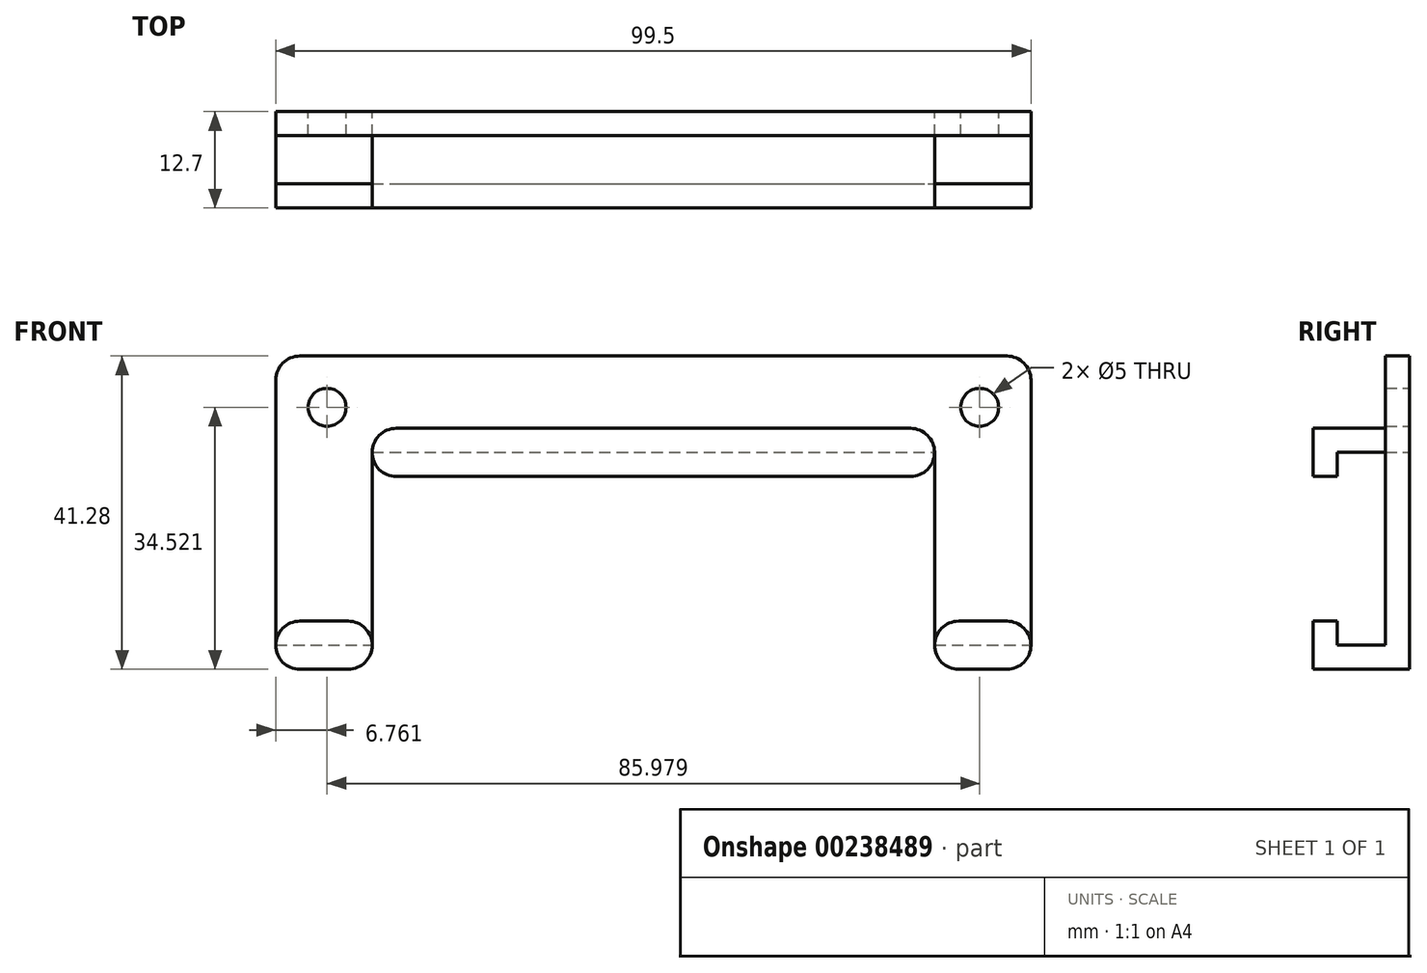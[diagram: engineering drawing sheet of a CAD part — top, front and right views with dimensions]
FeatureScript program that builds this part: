
annotation { "Feature Type Name" : "Feature", "Feature Type Description" : "" }
export const myFeature = defineFeature(function(context is Context, id is Id, definition is map)
    precondition{}
    {
        {
            var Q0;
            Q0=qCreatedBy(makeId("Front.planeOp"),FACE);
            var sketch = newSketch(context, id + "F0", { "sketchPlane" : qUnion([Q0])});
            skLineSegment(sketch, "E0.bottom", {"start": v(-49.75, 20.64) * mm, "end": v(49.75, 20.64) * mm});
            skLineSegment(sketch, "E0.left", {"start": v(-49.75, 20.64) * mm, "end": v(-49.75, -20.64) * mm});
            skLineSegment(sketch, "E0.right", {"start": v(49.75, 20.64) * mm, "end": v(49.75, -20.64) * mm});
            skPoint(sketch, "E0.middle", {"position": v(0, 0) * mm});
            skLineSegment(sketch, "E1", {"start": v(-49.75, -20.64) * mm, "end": v(-37.05, -20.64) * mm});
            skLineSegment(sketch, "E2", {"start": v(49.75, -20.64) * mm, "end": v(37.05, -20.64) * mm});
            skLineSegment(sketch, "E3", {"start": v(-37.05, -20.64) * mm, "end": v(-37.05, 7.94) * mm});
            skLineSegment(sketch, "E4", {"start": v(37.05, -20.64) * mm, "end": v(37.05, 7.94) * mm});
            skLineSegment(sketch, "E5", {"start": v(-37.05, 7.94) * mm, "end": v(37.05, 7.94) * mm});
            skLineSegment(sketch, "E6.bottom", {"start": v(-49.75, 20.64) * mm, "end": v(-42.99, 20.64) * mm, "construction": true});
            skLineSegment(sketch, "E6.top", {"start": v(-49.75, 13.88) * mm, "end": v(-42.99, 13.88) * mm, "construction": true});
            skLineSegment(sketch, "E6.left", {"start": v(-49.75, 20.64) * mm, "end": v(-49.75, 13.88) * mm, "construction": true});
            skLineSegment(sketch, "E6.right", {"start": v(-42.99, 20.64) * mm, "end": v(-42.99, 13.88) * mm, "construction": true});
            skLineSegment(sketch, "E7.bottom", {"start": v(49.75, 20.64) * mm, "end": v(42.99, 20.64) * mm, "construction": true});
            skLineSegment(sketch, "E7.top", {"start": v(49.75, 13.88) * mm, "end": v(42.99, 13.88) * mm, "construction": true});
            skLineSegment(sketch, "E7.left", {"start": v(49.75, 20.64) * mm, "end": v(49.75, 13.88) * mm, "construction": true});
            skLineSegment(sketch, "E7.right", {"start": v(42.99, 20.64) * mm, "end": v(42.99, 13.88) * mm, "construction": true});
            skCircle(sketch, "E8", {"center": v(-42.99, 13.88) * mm, "radius": 2.5 * mm});
            skCircle(sketch, "E9", {"center": v(42.99, 13.88) * mm, "radius": 2.5 * mm});
            skSolve(sketch);
        }
        {
            var Q0;
            Q0=makeQuery(id+"F0.imprint","IMPRINT",FACE,{"disambiguationData":[TD([[makeQuery(id+"F0.imprint","IMPRINT",EDGE,{"derivedFrom":sQuery(id+"F0.wireOp",EDGE,"BnNzGfss-3wFV-08qL-6QTv-cbIZqPfvRORX.bottom")}),1.0]])]});
            var Q1;
            Q1=makeQuery(id+"F0.imprint","IMPRINT",FACE,{"disambiguationData":[TD([[makeQuery(id+"F0.imprint","IMPRINT",EDGE,{"derivedFrom":sQuery(id+"F0.wireOp",EDGE,"E0.bottom")}),-1.0]])]});
            extrude(context, id + "F1", {"entities" : qUnion([Q0, Q1]), "depth" : 3.17 * mm});
        }
        {
            var Q0;
            Q0=makeQuery(id+"F1.opExtrude","CAP_FACE",FACE,{"disambiguationData":[OSD([sQuery(id+"F0.wireOp",EDGE,"E0.bottom"),sQuery(id+"F0.wireOp",EDGE,"E0.left"),sQuery(id+"F0.wireOp",EDGE,"E0.right"),sQuery(id+"F0.wireOp",EDGE,"E1"),sQuery(id+"F0.wireOp",EDGE,"E2"),sQuery(id+"F0.wireOp",EDGE,"E3"),sQuery(id+"F0.wireOp",EDGE,"E4"),sQuery(id+"F0.wireOp",EDGE,"E5"),sQuery(id+"F0.wireOp",EDGE,"E8"),sQuery(id+"F0.wireOp",EDGE,"E9")])],"isStart":false});
            var sketch = newSketch(context, id + "F2", { "sketchPlane" : qUnion([Q0])});
            skLineSegment(sketch, "E10.bottom", {"start": v(-49.75, -20.64) * mm, "end": v(-37.05, -20.64) * mm});
            skLineSegment(sketch, "E10.top", {"start": v(-49.75, -17.46) * mm, "end": v(-37.05, -17.46) * mm});
            skLineSegment(sketch, "E10.left", {"start": v(-49.75, -20.64) * mm, "end": v(-49.75, -17.46) * mm});
            skLineSegment(sketch, "E10.right", {"start": v(-37.05, -20.64) * mm, "end": v(-37.05, -17.46) * mm});
            skLineSegment(sketch, "E11.bottom", {"start": v(37.05, -20.64) * mm, "end": v(49.75, -20.64) * mm});
            skLineSegment(sketch, "E11.top", {"start": v(37.05, -17.46) * mm, "end": v(49.75, -17.46) * mm});
            skLineSegment(sketch, "E11.left", {"start": v(37.05, -20.64) * mm, "end": v(37.05, -17.46) * mm});
            skLineSegment(sketch, "E11.right", {"start": v(49.75, -20.64) * mm, "end": v(49.75, -17.46) * mm});
            skLineSegment(sketch, "E12.bottom", {"start": v(37.05, 7.94) * mm, "end": v(-37.05, 7.94) * mm});
            skLineSegment(sketch, "E12.top", {"start": v(37.05, 11.11) * mm, "end": v(-37.05, 11.11) * mm});
            skLineSegment(sketch, "E12.left", {"start": v(37.05, 7.94) * mm, "end": v(37.05, 11.11) * mm});
            skLineSegment(sketch, "E12.right", {"start": v(-37.05, 7.94) * mm, "end": v(-37.05, 11.11) * mm});
            skSolve(sketch);
        }
        {
            var Q0;
            Q0=makeQuery(id+"F2.imprint","IMPRINT",FACE,{"disambiguationData":[TD([[makeQuery(id+"F2.imprint","IMPRINT",EDGE,{"derivedFrom":sQuery(id+"F2.wireOp",EDGE,"E10.bottom")}),1.0]])]});
            var Q1;
            Q1=makeQuery(id+"F2.imprint","IMPRINT",FACE,{"disambiguationData":[TD([[makeQuery(id+"F2.imprint","IMPRINT",EDGE,{"derivedFrom":sQuery(id+"F2.wireOp",EDGE,"E12.bottom")}),1.0]])]});
            var Q2;
            Q2=makeQuery(id+"F2.imprint","IMPRINT",FACE,{"disambiguationData":[TD([[makeQuery(id+"F2.imprint","IMPRINT",EDGE,{"derivedFrom":sQuery(id+"F2.wireOp",EDGE,"E11.bottom")}),-1.0]])]});
            extrude(context, id + "F3", {"entities" : qUnion([Q0, Q1, Q2]), "operationType" : NewBodyOperationType.ADD, "depth" : 9.52 * mm});
        }
        {
            var Q0;
            Q0=makeQuery(id+"F3.opExtrude","SWEPT_FACE",FACE,{"disambiguationData":[OSD([sQuery(id+"F2.wireOp",EDGE,"E10.top")])]});
            var sketch = newSketch(context, id + "F4", { "sketchPlane" : qUnion([Q0])});
            skLineSegment(sketch, "E13.bottom", {"start": v(-37.05, -12.7) * mm, "end": v(-49.75, -12.7) * mm});
            skLineSegment(sketch, "E13.top", {"start": v(-37.05, -9.53) * mm, "end": v(-49.75, -9.53) * mm});
            skLineSegment(sketch, "E13.left", {"start": v(-37.05, -12.7) * mm, "end": v(-37.05, -9.52) * mm});
            skLineSegment(sketch, "E13.right", {"start": v(-49.75, -12.7) * mm, "end": v(-49.75, -9.53) * mm});
            skSolve(sketch);
        }
        {
            var Q0;
            Q0=makeQuery(id+"F3.opExtrude","SWEPT_FACE",FACE,{"disambiguationData":[OSD([sQuery(id+"F2.wireOp",EDGE,"E11.top")])]});
            var sketch = newSketch(context, id + "F5", { "sketchPlane" : qUnion([Q0])});
            skLineSegment(sketch, "E14.bottom", {"start": v(49.75, -12.7) * mm, "end": v(37.05, -12.7) * mm});
            skLineSegment(sketch, "E14.top", {"start": v(49.75, -9.53) * mm, "end": v(37.05, -9.53) * mm});
            skLineSegment(sketch, "E14.left", {"start": v(49.75, -12.7) * mm, "end": v(49.75, -9.53) * mm});
            skLineSegment(sketch, "E14.right", {"start": v(37.05, -12.7) * mm, "end": v(37.05, -9.53) * mm});
            skSolve(sketch);
        }
        {
            var Q0;
            Q0=makeQuery(id+"F4.imprint","IMPRINT",FACE,{"disambiguationData":[TD([[makeQuery(id+"F4.imprint","IMPRINT",EDGE,{"derivedFrom":sQuery(id+"F4.wireOp",EDGE,"E13.bottom")}),1.0]])]});
            var Q1;
            Q1=makeQuery(id+"F5.imprint","IMPRINT",FACE,{"disambiguationData":[TD([[makeQuery(id+"F5.imprint","IMPRINT",EDGE,{"derivedFrom":sQuery(id+"F5.wireOp",EDGE,"E14.bottom")}),1.0]])]});
            extrude(context, id + "F6", {"entities" : qUnion([Q0, Q1]), "operationType" : NewBodyOperationType.ADD, "depth" : 3.17 * mm});
        }
        {
            var Q0;
            Q0=makeQuery(id+"F3.boolean.opBoolean","MERGE",FACE,{"derivedFrom":[makeQuery(id+"F1.opExtrude","SWEPT_FACE",FACE,{"disambiguationData":[OSD([sQuery(id+"F0.wireOp",EDGE,"E5")])]}),makeQuery(id+"F3.opExtrude","SWEPT_FACE",FACE,{"disambiguationData":[OSD([sQuery(id+"F2.wireOp",EDGE,"E12.bottom")])]})]});
            var sketch = newSketch(context, id + "F7", { "sketchPlane" : qUnion([Q0])});
            skLineSegment(sketch, "E15.bottom", {"start": v(-37.05, 12.7) * mm, "end": v(37.05, 12.7) * mm});
            skLineSegment(sketch, "E15.top", {"start": v(-37.05, 9.53) * mm, "end": v(37.05, 9.53) * mm});
            skLineSegment(sketch, "E15.left", {"start": v(-37.05, 12.7) * mm, "end": v(-37.05, 9.53) * mm});
            skLineSegment(sketch, "E15.right", {"start": v(37.05, 12.7) * mm, "end": v(37.05, 9.53) * mm});
            skSolve(sketch);
        }
        {
            var Q0;
            Q0=makeQuery(id+"F7.imprint","IMPRINT",FACE,{"disambiguationData":[TD([[makeQuery(id+"F7.imprint","IMPRINT",EDGE,{"derivedFrom":sQuery(id+"F7.wireOp",EDGE,"E15.bottom")}),-1.0]])]});
            extrude(context, id + "F8", {"entities" : qUnion([Q0]), "operationType" : NewBodyOperationType.ADD, "depth" : 3.17 * mm});
        }
        {
            var Q0;
            Q0=makeQuery(id+"F1.opExtrude","SWEPT_EDGE",EDGE,{"disambiguationData":[OSD([sQuery(id+"F0.wireOp",EDGE,"E0.bottom"),sQuery(id+"F0.wireOp",EDGE,"E0.left")])]});
            var Q1;
            Q1=makeQuery(id+"F3.boolean.opBoolean","MERGE",EDGE,{"derivedFrom":[makeQuery(id+"F1.opExtrude","SWEPT_EDGE",EDGE,{"disambiguationData":[OSD([sQuery(id+"F0.wireOp",EDGE,"E0.left"),sQuery(id+"F0.wireOp",EDGE,"E1")])]}),makeQuery(id+"F3.opExtrude","SWEPT_EDGE",EDGE,{"disambiguationData":[OSD([sQuery(id+"F2.wireOp",EDGE,"E10.bottom"),sQuery(id+"F2.wireOp",EDGE,"E10.left")])]})]});
            var Q2;
            Q2=makeQuery(id+"F6.opExtrude","CAP_EDGE",EDGE,{"disambiguationData":[OSD([sQuery(id+"F4.wireOp",EDGE,"E13.right")])],"isStart":false});
            var Q3;
            Q3=makeQuery(id+"F3.opExtrude","SWEPT_EDGE",EDGE,{"disambiguationData":[OSD([sQuery(id+"F2.wireOp",EDGE,"E12.top"),sQuery(id+"F2.wireOp",EDGE,"E12.right")])]});
            var Q4;
            Q4=makeQuery(id+"F8.opExtrude","CAP_EDGE",EDGE,{"disambiguationData":[OSD([sQuery(id+"F7.wireOp",EDGE,"E15.left")])],"isStart":false});
            var Q5;
            Q5=makeQuery(id+"F6.opExtrude","CAP_EDGE",EDGE,{"disambiguationData":[OSD([sQuery(id+"F4.wireOp",EDGE,"E13.left")])],"isStart":false});
            var Q6;
            Q6=makeQuery(id+"F3.boolean.opBoolean","MERGE",EDGE,{"derivedFrom":[makeQuery(id+"F1.opExtrude","SWEPT_EDGE",EDGE,{"disambiguationData":[OSD([sQuery(id+"F0.wireOp",EDGE,"E1"),sQuery(id+"F0.wireOp",EDGE,"E3")])]}),makeQuery(id+"F3.opExtrude","SWEPT_EDGE",EDGE,{"disambiguationData":[OSD([sQuery(id+"F2.wireOp",EDGE,"E10.bottom"),sQuery(id+"F2.wireOp",EDGE,"E10.right")])]})]});
            var Q7;
            Q7=makeQuery(id+"F1.opExtrude","SWEPT_EDGE",EDGE,{"disambiguationData":[OSD([sQuery(id+"F0.wireOp",EDGE,"E0.bottom"),sQuery(id+"F0.wireOp",EDGE,"E0.right")])]});
            var Q8;
            Q8=makeQuery(id+"F3.boolean.opBoolean","MERGE",EDGE,{"derivedFrom":[makeQuery(id+"F1.opExtrude","SWEPT_EDGE",EDGE,{"disambiguationData":[OSD([sQuery(id+"F0.wireOp",EDGE,"E0.right"),sQuery(id+"F0.wireOp",EDGE,"E2")])]}),makeQuery(id+"F3.opExtrude","SWEPT_EDGE",EDGE,{"disambiguationData":[OSD([sQuery(id+"F2.wireOp",EDGE,"E11.bottom"),sQuery(id+"F2.wireOp",EDGE,"E11.right")])]})]});
            var Q9;
            Q9=makeQuery(id+"F3.opExtrude","SWEPT_EDGE",EDGE,{"disambiguationData":[OSD([sQuery(id+"F2.wireOp",EDGE,"E12.top"),sQuery(id+"F2.wireOp",EDGE,"E12.left")])]});
            var Q10;
            Q10=makeQuery(id+"F8.opExtrude","CAP_EDGE",EDGE,{"disambiguationData":[OSD([sQuery(id+"F7.wireOp",EDGE,"E15.right")])],"isStart":false});
            var Q11;
            Q11=makeQuery(id+"F6.opExtrude","CAP_EDGE",EDGE,{"disambiguationData":[OSD([sQuery(id+"F5.wireOp",EDGE,"E14.right")])],"isStart":false});
            var Q12;
            Q12=makeQuery(id+"F3.boolean.opBoolean","MERGE",EDGE,{"derivedFrom":[makeQuery(id+"F1.opExtrude","SWEPT_EDGE",EDGE,{"disambiguationData":[OSD([sQuery(id+"F0.wireOp",EDGE,"E2"),sQuery(id+"F0.wireOp",EDGE,"E4")])]}),makeQuery(id+"F3.opExtrude","SWEPT_EDGE",EDGE,{"disambiguationData":[OSD([sQuery(id+"F2.wireOp",EDGE,"E11.bottom"),sQuery(id+"F2.wireOp",EDGE,"E11.left")])]})]});
            var Q13;
            Q13=makeQuery(id+"F6.opExtrude","CAP_EDGE",EDGE,{"disambiguationData":[OSD([sQuery(id+"F5.wireOp",EDGE,"E14.left")])],"isStart":false});
            fillet(context, id + "F9", {"entities" : qUnion([Q0, Q1, Q2, Q3, Q4, Q5, Q6, Q7, Q8, Q9, Q10, Q11, Q12, Q13]), "radius" : 3.17 * mm, "tangentPropagation" : true, "allowEdgeOverflow" : false});
        }
    });
